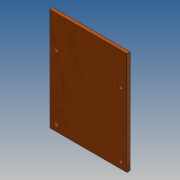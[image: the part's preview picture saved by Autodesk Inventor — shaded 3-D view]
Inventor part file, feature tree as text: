
AUTODESK INVENTOR PART (.ipt)
format: ipt  version: 2017 (Build 210142000, 142)  size: 95,232 bytes
history: native  units: mm
features: other x1, extrude x1, sketch x1
ambient origin geometry x8: Origin, YZ Plane, XZ Plane, XY Plane, X Axis, Y Axis, Z Axis, Center Point
bodies: Body1 (feature_tree)
feature tree (3):
  other  "Sólido1"
  extrude  "Extrusión1"  Depth=80.0mm
  sketch  "Boceto1"  dims[d0=3.0mm d1=80.0mm d2=5.0mm d3=2.5mm d4=0.0mm d5=60.0mm d6=20.0mm d7=15.0mm]
